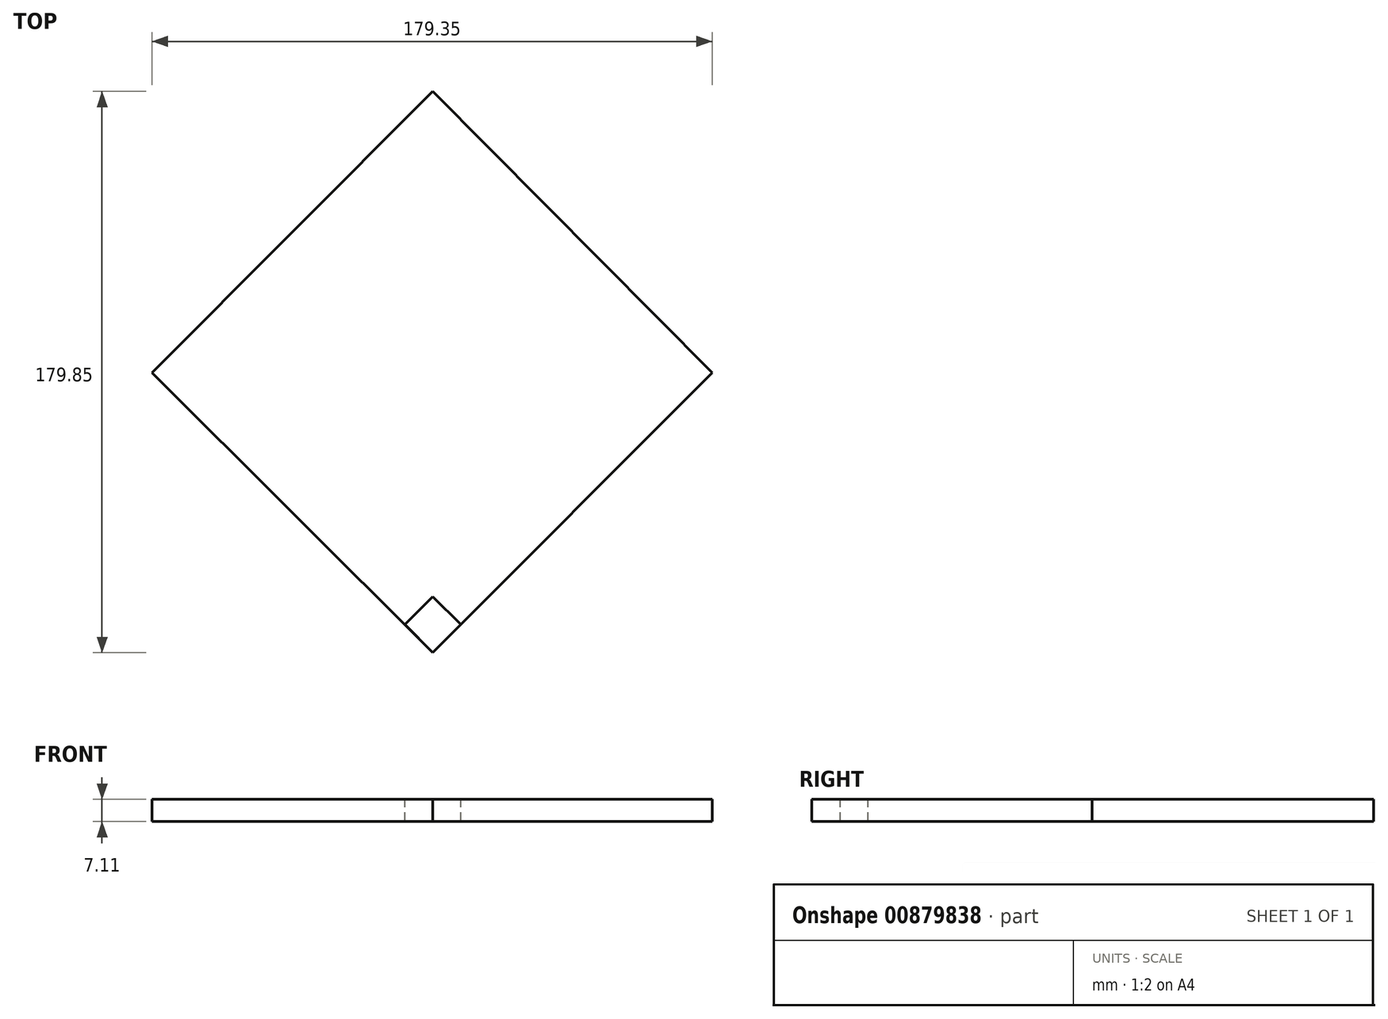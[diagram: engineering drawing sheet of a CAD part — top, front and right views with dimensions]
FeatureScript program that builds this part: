
annotation { "Feature Type Name" : "Feature", "Feature Type Description" : "" }
export const myFeature = defineFeature(function(context is Context, id is Id, definition is map)
    precondition{}
    {
        {
            var Q0;
            Q0=qCreatedBy(makeId("Top.planeOp"),FACE);
            var sketch = newSketch(context, id + "F0", { "sketchPlane" : qUnion([Q0])});
            skLineSegment(sketch, "E0", {"start": v(0, 90.18) * mm, "end": v(-89.93, 0) * mm});
            skLineSegment(sketch, "E1", {"start": v(-89.93, 0) * mm, "end": v(0, -89.67) * mm});
            skLineSegment(sketch, "E2", {"start": v(0, -89.67) * mm, "end": v(89.42, 0) * mm});
            skLineSegment(sketch, "E3", {"start": v(89.42, 0) * mm, "end": v(0, 90.18) * mm});
            skSolve(sketch);
        }
        {
            var Q0;
            Q0=makeQuery(id+"F0.imprint","IMPRINT",FACE,{"disambiguationData":[TD([[makeQuery(id+"F0.imprint","IMPRINT",EDGE,{"derivedFrom":sQuery(id+"F0.wireOp",EDGE,"E0")}),1.0]])]});
            var sketch = newSketch(context, id + "F1", { "sketchPlane" : qUnion([Q0])});
            skLineSegment(sketch, "E4", {"start": v(0, 90.2) * mm, "end": v(-9.15, 81) * mm});
            skLineSegment(sketch, "E5", {"start": v(-9.15, 81) * mm, "end": v(0, 71.91) * mm});
            skLineSegment(sketch, "E6", {"start": v(0, 71.91) * mm, "end": v(9.03, 81) * mm});
            skLineSegment(sketch, "E7", {"start": v(9.03, 81) * mm, "end": v(0, 90.2) * mm});
            skSolve(sketch);
        }
        {
            var Q0;
            Q0=makeQuery(id+"F0.imprint","IMPRINT",FACE,{"disambiguationData":[TD([[makeQuery(id+"F0.imprint","IMPRINT",EDGE,{"derivedFrom":sQuery(id+"F0.wireOp",EDGE,"E0")}),1.0]])]});
            var sketch = newSketch(context, id + "F2", { "sketchPlane" : qUnion([Q0])});
            skLineSegment(sketch, "E8", {"start": v(0, -89.65) * mm, "end": v(8.99, -80.63) * mm});
            skLineSegment(sketch, "E9", {"start": v(8.99, -80.63) * mm, "end": v(0, -71.68) * mm});
            skLineSegment(sketch, "E10", {"start": v(0, -71.68) * mm, "end": v(-8.93, -80.63) * mm});
            skLineSegment(sketch, "E11", {"start": v(-8.93, -80.63) * mm, "end": v(0, -89.65) * mm});
            skSolve(sketch);
        }
        {
            var Q0;
            Q0=sQuery(id+"F1.wireOp",EDGE,"E6");
            var Q1;
            Q1=sQuery(id+"F1.wireOp",EDGE,"E5");
            var Q2;
            Q2=sQuery(id+"F1.wireOp",EDGE,"E4");
            var Q3;
            Q3=sQuery(id+"F1.wireOp",EDGE,"E7");
            extrude(context, id + "F3", {"bodyType" : ToolBodyType.SURFACE, "surfaceEntities" : qUnion([Q0, Q1, Q2, Q3]), "depth" : 25.4 * mm, "offsetDistance" : 25.4 * mm});
        }
        {
            var Q0;
            Q0=makeQuery(id+"F2.imprint","IMPRINT",FACE,{"disambiguationData":[TD([[makeQuery(id+"F2.imprint","IMPRINT",EDGE,{"derivedFrom":sQuery(id+"F2.wireOp",EDGE,"E8")}),-1.0]])]});
            var Q1;
            Q1=makeQuery(id+"F0.imprint","IMPRINT",FACE,{"disambiguationData":[TD([[makeQuery(id+"F0.imprint","IMPRINT",EDGE,{"derivedFrom":sQuery(id+"F0.wireOp",EDGE,"E0")}),1.0]])]});
            extrude(context, id + "F4", {"entities" : qUnion([Q0, Q1]), "oppositeDirection" : true, "depth" : 7.11 * mm, "offsetDistance" : 25.4 * mm});
        }
    });
